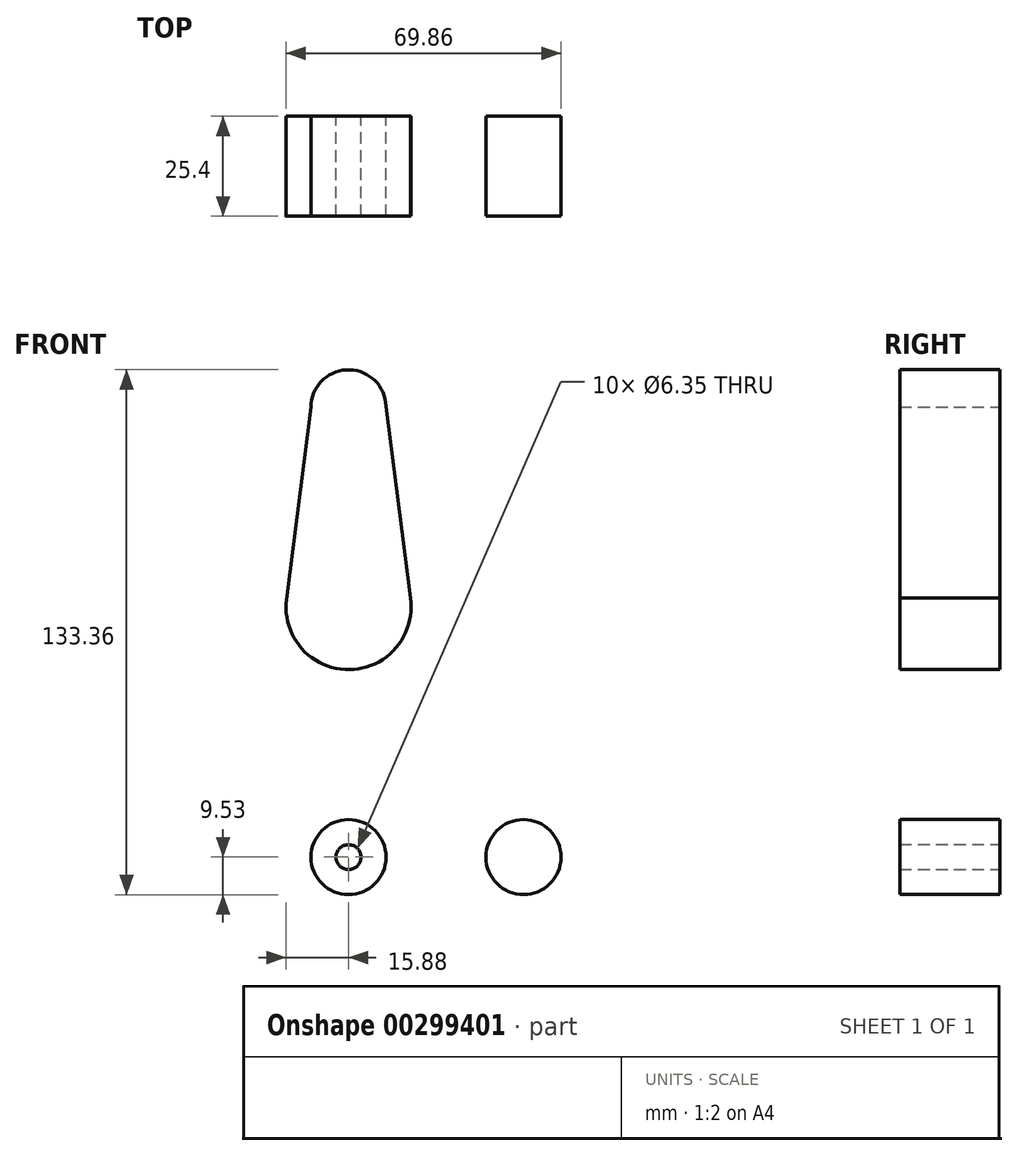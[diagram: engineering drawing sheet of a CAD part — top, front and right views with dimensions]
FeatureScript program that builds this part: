
annotation { "Feature Type Name" : "Feature", "Feature Type Description" : "" }
export const myFeature = defineFeature(function(context is Context, id is Id, definition is map)
    precondition{}
    {
        {
            var Q0;
            Q0=qCreatedBy(makeId("Front.planeOp"),FACE);
            var sketch = newSketch(context, id + "F0", { "sketchPlane" : qUnion([Q0])});
            skCircle(sketch, "E0", {"center": v(0, 0) * mm, "radius": 9.53 * mm});
            skCircle(sketch, "E1", {"center": v(0, 63.5) * mm, "radius": 15.88 * mm});
            skCircle(sketch, "E2", {"center": v(0, 114.3) * mm, "radius": 9.53 * mm});
            skCircle(sketch, "E3", {"center": v(44.45, 0) * mm, "radius": 9.53 * mm});
            skLineSegment(sketch, "E4", {"start": v(-9.53, 114.3) * mm, "end": v(-15.75, 65.5) * mm});
            skPoint(sketch, "E5.newPointA", {"position": v(-1.55, 0) * mm});
            skPoint(sketch, "E5.newPointB", {"position": v(0, 9.53) * mm});
            skLineSegment(sketch, "E6", {"start": v(44.24, -9.52) * mm, "end": v(0, -9.53) * mm});
            skLineSegment(sketch, "E7", {"start": v(15.8, 65.1) * mm, "end": v(9.45, 115.49) * mm});
            skLineSegment(sketch, "E8", {"start": v(15.8, 63.5) * mm, "end": v(11.36, 18.25) * mm});
            skLineSegment(sketch, "E9", {"start": v(19.27, 9.53) * mm, "end": v(44.45, 9.53) * mm});
            skPoint(sketch, "E10.newPointA", {"position": v(9.57, 0) * mm});
            skArc(sketch, "E10.filletArc", {"start": v(11.36, 18.25) * mm, "mid": v(13.38, 12.14) * mm, "end": v(19.27, 9.53) * mm});
            skCircle(sketch, "E11", {"center": v(-7.15, 100.03) * mm, "radius": 2.94 * mm});
            skLineSegment(sketch, "E12", {"start": v(-15.8, 61.91) * mm, "end": v(-9.48, -0.95) * mm});
            skCircle(sketch, "E13", {"center": v(0, 114.3) * mm, "radius": 3.18 * mm});
            skCircle(sketch, "E14", {"center": v(0, 63.5) * mm, "radius": 3.18 * mm});
            skCircle(sketch, "E15", {"center": v(0, 0) * mm, "radius": 3.18 * mm});
            skCircle(sketch, "E16", {"center": v(44.45, 0) * mm, "radius": 3.18 * mm});
            skSolve(sketch);
        }
        {
            var Q0;
            Q0 = qSketchRegion(id + "F0", true);
            extrude(context, id + "F1", {"entities" : qUnion([Q0]), "depth" : 25.4 * mm});
        }
    });
